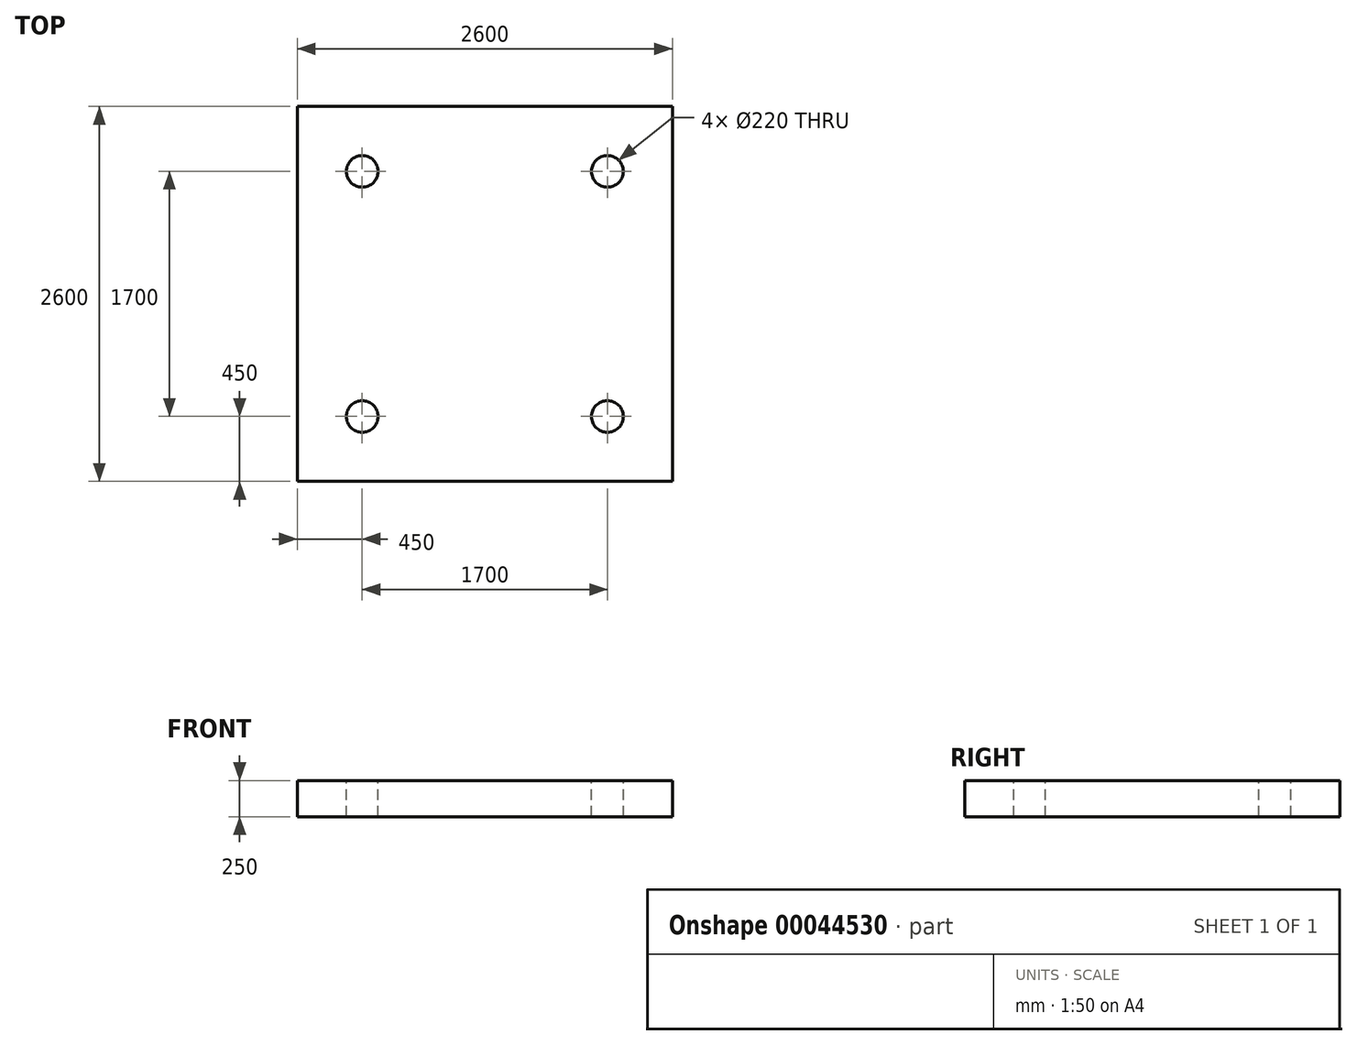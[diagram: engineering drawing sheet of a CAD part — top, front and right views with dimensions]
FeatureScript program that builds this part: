
annotation { "Feature Type Name" : "Feature", "Feature Type Description" : "" }
export const myFeature = defineFeature(function(context is Context, id is Id, definition is map)
    precondition{}
    {
        {
            var Q0;
            Q0=qCreatedBy(makeId("Top.planeOp"),FACE);
            var sketch = newSketch(context, id + "F0", { "sketchPlane" : qUnion([Q0])});
            skLineSegment(sketch, "E0.rect.bottom", {"start": v(-1300, 1300) * mm, "end": v(1300, 1300) * mm});
            skLineSegment(sketch, "E0.rect.top", {"start": v(-1300, -1300) * mm, "end": v(1300, -1300) * mm});
            skLineSegment(sketch, "E0.rect.left", {"start": v(-1300, 1300) * mm, "end": v(-1300, -1300) * mm});
            skLineSegment(sketch, "E0.rect.right", {"start": v(1300, 1300) * mm, "end": v(1300, -1300) * mm});
            skPoint(sketch, "E0.rect.middle", {"position": v(0, 0) * mm});
            skSolve(sketch);
        }
        {
            var Q0;
            Q0 = qSketchRegion(id + "F0", true);
            extrude(context, id + "F1", {"entities" : qUnion([Q0]), "depth" : 250 * mm});
        }
        {
            var Q0;
            Q0=makeQuery(id+"F1.opExtrude","CAP_FACE",FACE,{"disambiguationData":[OSD([sQuery(id+"F0.wireOp",EDGE,"E0.rect.bottom"),sQuery(id+"F0.wireOp",EDGE,"E0.rect.top"),sQuery(id+"F0.wireOp",EDGE,"E0.rect.left"),sQuery(id+"F0.wireOp",EDGE,"E0.rect.right")])],"isStart":false});
            var sketch = newSketch(context, id + "F2", { "sketchPlane" : qUnion([Q0])});
            skCircle(sketch, "E1", {"center": v(-850, 850) * mm, "radius": 110 * mm});
            skLineSegment(sketch, "E2", {"start": v(0, 1542.89) * mm, "end": v(0, -1625.23) * mm, "construction": true});
            skLineSegment(sketch, "E3", {"start": v(1864.36, 0) * mm, "end": v(-1748.57, 0) * mm, "construction": true});
            skCircle(sketch, "E4.MirrorC", {"center": v(850, 850) * mm, "radius": 110 * mm});
            skCircle(sketch, "E5.MirrorC", {"center": v(-850, -850) * mm, "radius": 110 * mm});
            skCircle(sketch, "E6.MirrorC", {"center": v(850, -850) * mm, "radius": 110 * mm});
            skSolve(sketch);
        }
        {
            var Q0;
            Q0 = qSketchRegion(id + "F2", true);
            extrude(context, id + "F3", {"entities" : qUnion([Q0]), "operationType" : NewBodyOperationType.REMOVE, "oppositeDirection" : true, "depth" : 1000 * mm});
        }
    });
